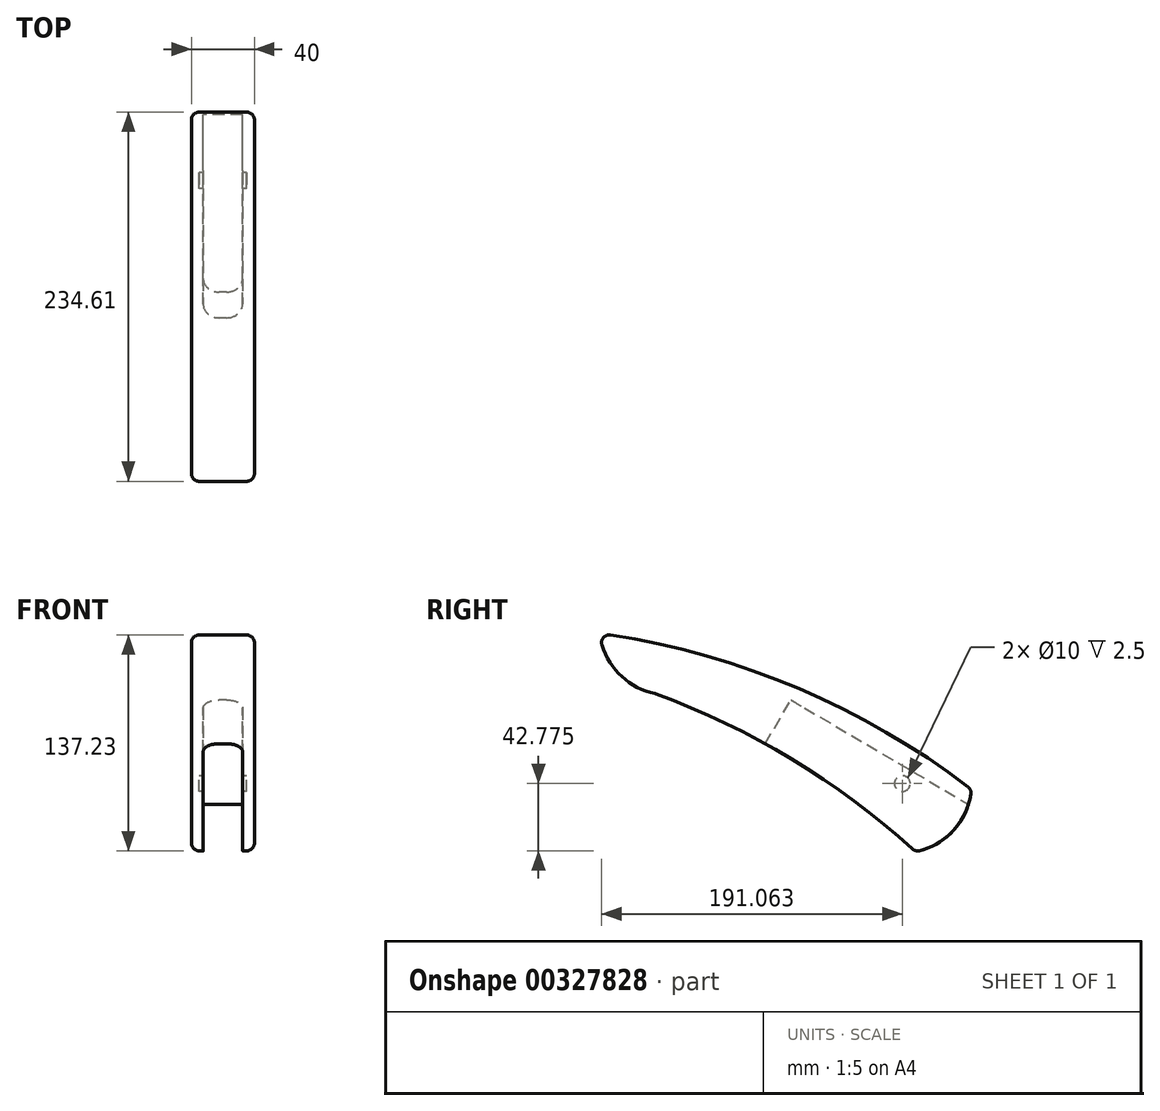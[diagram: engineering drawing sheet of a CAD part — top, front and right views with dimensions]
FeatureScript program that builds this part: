
annotation { "Feature Type Name" : "Feature", "Feature Type Description" : "" }
export const myFeature = defineFeature(function(context is Context, id is Id, definition is map)
    precondition{}
    {
        {
            var Q0;
            Q0=qCreatedBy(makeId("Right.planeOp"),FACE);
            var sketch = newSketch(context, id + "F0", { "sketchPlane" : qUnion([Q0])});
            skLineSegment(sketch, "E0.bottom", {"start": v(-93.5, -201.38) * mm, "end": v(36.5, -201.38) * mm});
            skLineSegment(sketch, "E0.top", {"start": v(-93.5, 198.62) * mm, "end": v(36.5, 198.62) * mm});
            skLineSegment(sketch, "E0.left", {"start": v(-93.5, -201.38) * mm, "end": v(-93.5, 198.62) * mm});
            skLineSegment(sketch, "E0.right", {"start": v(36.5, -201.38) * mm, "end": v(36.5, 198.62) * mm});
            skCircle(sketch, "E1", {"center": v(-63.5, -21.38) * mm, "radius": 5 * mm});
            skCircle(sketch, "E2", {"center": v(-13.5, 168.62) * mm, "radius": 5 * mm});
            skLineSegment(sketch, "E3", {"start": v(-63.5, -21.38) * mm, "end": v(-15.78, 249.23) * mm, "construction": true});
            skSolve(sketch);
        }
        {
            var Q0;
            Q0=makeQuery(id+"F0.imprint","IMPRINT",FACE,{"disambiguationData":[TD([[makeQuery(id+"F0.imprint","IMPRINT",EDGE,{"derivedFrom":sQuery(id+"F0.wireOp",EDGE,"E0.bottom")}),1.0]])]});
            var sketch = newSketch(context, id + "F1", { "sketchPlane" : qUnion([Q0])});
            skArc(sketch, "E4", {"start": v(-83.4, -179.38) * mm, "mid": v(-76.66, -2.28) * mm, "end": v(-91.76, 174.32) * mm});
            skArc(sketch, "E5", {"start": v(-4.63, -188.02) * mm, "mid": v(29.08, -8.61) * mm, "end": v(7.29, 172.63) * mm});
            skArc(sketch, "E6", {"start": v(-7.3, 186.7) * mm, "mid": v(-38.5, 193.04) * mm, "end": v(-70.09, 197.16) * mm});
            skPoint(sketch, "E7.orphan", {"position": v(0, 196.75) * mm});
            skPoint(sketch, "E8.orphan", {"position": v(0, -174.33) * mm});
            skPoint(sketch, "E9.visualSharp", {"position": v(-10.38, -203.65) * mm});
            skArc(sketch, "E9.filletArc", {"start": v(-23.5, -201.38) * mm, "mid": v(-11.94, -197.7) * mm, "end": v(-4.63, -188.02) * mm});
            skPoint(sketch, "E10.visualSharp", {"position": v(4.05, 183.8) * mm});
            skArc(sketch, "E10.filletArc", {"start": v(7.29, 172.63) * mm, "mid": v(1.9, 181.64) * mm, "end": v(-7.3, 186.7) * mm});
            skPoint(sketch, "E11.visualSharp", {"position": v(-95.6, 198.84) * mm});
            skArc(sketch, "E11.filletArc", {"start": v(-70.09, 197.16) * mm, "mid": v(-86.48, 191.01) * mm, "end": v(-91.76, 174.32) * mm});
            skPoint(sketch, "E12.visualSharp", {"position": v(-89.2, -228.69) * mm});
            skArc(sketch, "E12.filletArc", {"start": v(-83.4, -179.38) * mm, "mid": v(-78.33, -194.8) * mm, "end": v(-63.5, -201.38) * mm});
            skLineSegment(sketch, "E13", {"start": v(-63.5, -201.38) * mm, "end": v(-23.5, -201.38) * mm});
            skSolve(sketch);
        }
        {
            var Q0;
            Q0=makeQuery(id+"F0.imprint","IMPRINT",FACE,{"disambiguationData":[TD([[makeQuery(id+"F0.imprint","IMPRINT",EDGE,{"derivedFrom":sQuery(id+"F0.wireOp",EDGE,"E0.bottom")}),1.0]])]});
            var sketch = newSketch(context, id + "F2", { "sketchPlane" : qUnion([Q0])});
            skArc(sketch, "E14", {"start": v(-5.24, 125.4) * mm, "mid": v(-82.88, 183.6) * mm, "end": v(-170.3, 225.71) * mm});
            skArc(sketch, "E15", {"start": v(30.35, 164.93) * mm, "mid": v(-81.33, 229.89) * mm, "end": v(-205.92, 264.07) * mm});
            skArc(sketch, "E16", {"start": v(-205.92, 264.07) * mm, "mid": v(-194.3, 239.14) * mm, "end": v(-170.3, 225.71) * mm});
            skCircle(sketch, "E17", {"center": v(-13.5, 168.62) * mm, "radius": 5 * mm, "construction": true});
            skArc(sketch, "E18", {"start": v(-5.24, 125.4) * mm, "mid": v(19.2, 139.18) * mm, "end": v(30.35, 164.93) * mm});
            skPoint(sketch, "E19.orphan", {"position": v(0, 120.54) * mm});
            skSolve(sketch);
        }
        {
            var Q0;
            Q0=makeQuery(id+"F2.imprint","IMPRINT",FACE,{"disambiguationData":[TD([[makeQuery(id+"F2.imprint","IMPRINT",EDGE,{"derivedFrom":makeQuery(id+"F0.imprint","IMPRINT",EDGE,{"derivedFrom":sQuery(id+"F0.wireOp",EDGE,"E2")})}),1.0]])]});
            var Q1;
            {var subQ0=sQuery(id+"F2.wireOp",EDGE,"vNOhyl8z-5HtI-Y5xh-fr09-2KdCwjozxGuU");Q1=makeQuery(id+"F2.imprint","IMPRINT",FACE,{"disambiguationData":[TD([[makeQuery(id+"F2.imprint","IMPRINT",EDGE,{"derivedFrom":subQ0}),1.0]])]});}
            var Q2;
            {var subQ0=sQuery(id+"F2.wireOp",EDGE,"E16");Q2=makeQuery(id+"F2.imprint","IMPRINT",FACE,{"disambiguationData":[TD([[makeQuery(id+"F2.imprint","IMPRINT",EDGE,{"derivedFrom":subQ0}),1.0]])]});}
            var Q3;
            Q3=makeQuery(id+"F2.imprint","IMPRINT",FACE,{"disambiguationData":[TD([[makeQuery(id+"F2.imprint","IMPRINT",EDGE,{"derivedFrom":makeQuery(id+"F0.imprint","IMPRINT",EDGE,{"derivedFrom":sQuery(id+"F0.wireOp",EDGE,"E2")})}),-1.0]])]});
            extrude(context, id + "F3", {"entities" : qUnion([Q0, Q1, Q2, Q3]), "endBound" : BoundingType.SYMMETRIC, "depth" : 40 * mm, "offsetDistance" : 25 * mm});
        }
        {
            var Q0;
            Q0=makeQuery(id+"F3.opExtrude","CAP_FACE",FACE,{"disambiguationData":[OSD([sQuery(id+"F2.wireOp",EDGE,"E14"),sQuery(id+"F2.wireOp",EDGE,"E15"),sQuery(id+"F2.wireOp",EDGE,"E16"),sQuery(id+"F2.wireOp",EDGE,"vNOhyl8z-5HtI-Y5xh-fr09-2KdCwjozxGuU")])],"isStart":false});
            var Q1;
            Q1=makeQuery(id+"F3.opExtrude","CAP_FACE",FACE,{"disambiguationData":[OSD([sQuery(id+"F2.wireOp",EDGE,"E14"),sQuery(id+"F2.wireOp",EDGE,"E15"),sQuery(id+"F2.wireOp",EDGE,"E16"),sQuery(id+"F2.wireOp",EDGE,"vNOhyl8z-5HtI-Y5xh-fr09-2KdCwjozxGuU")])],"isStart":true});
            var Q2;
            Q2=makeQuery(id+"F3.opExtrude","SWEPT_EDGE",EDGE,{"disambiguationData":[OSD([sQuery(id+"F2.wireOp",EDGE,"E15"),sQuery(id+"F2.wireOp",EDGE,"vNOhyl8z-5HtI-Y5xh-fr09-2KdCwjozxGuU")])]});
            var Q3;
            Q3=makeQuery(id+"F3.opExtrude","SWEPT_EDGE",EDGE,{"disambiguationData":[OSD([sQuery(id+"F2.wireOp",EDGE,"E15"),sQuery(id+"F2.wireOp",EDGE,"E16")])]});
            var Q4;
            Q4=makeQuery(id+"F3.opExtrude","SWEPT_EDGE",EDGE,{"disambiguationData":[OSD([sQuery(id+"F2.wireOp",EDGE,"E14"),sQuery(id+"F2.wireOp",EDGE,"E16")])]});
            var Q5;
            Q5=makeQuery(id+"F3.opExtrude","SWEPT_EDGE",EDGE,{"disambiguationData":[OSD([sQuery(id+"F2.wireOp",EDGE,"E14"),sQuery(id+"F2.wireOp",EDGE,"vNOhyl8z-5HtI-Y5xh-fr09-2KdCwjozxGuU")])]});
            fillet(context, id + "F4", {"entities" : qUnion([Q0, Q1, Q2, Q3, Q4, Q5]), "radius" : 5 * mm, "tangentPropagation" : true, "allowEdgeOverflow" : false});
        }
        {
            var Q0;
            Q0=makeQuery(id+"F0.imprint","IMPRINT",FACE,{"disambiguationData":[TD([[makeQuery(id+"F0.imprint","IMPRINT",EDGE,{"derivedFrom":sQuery(id+"F0.wireOp",EDGE,"E0.bottom")}),1.0]])]});
            var sketch = newSketch(context, id + "F5", { "sketchPlane" : qUnion([Q0])});
            skCircle(sketch, "E20.0", {"center": v(-13.5, 168.62) * mm, "radius": 5 * mm});
            skSolve(sketch);
        }
        {
            var Q0;
            Q0 = qSketchRegion(id + "F5", true);
            extrude(context, id + "F6", {"entities" : qUnion([Q0]), "operationType" : NewBodyOperationType.REMOVE, "endBound" : BoundingType.SYMMETRIC, "depth" : 30 * mm, "offsetDistance" : 25 * mm});
        }
        {
            var Q0;
            Q0=makeQuery(id+"F3.opExtrude","CAP_FACE",FACE,{"disambiguationData":[OSD([sQuery(id+"F2.wireOp",EDGE,"E14"),sQuery(id+"F2.wireOp",EDGE,"E15"),sQuery(id+"F2.wireOp",EDGE,"E16"),sQuery(id+"F2.wireOp",EDGE,"E18")])],"isStart":false});
            cPlane(context, id + "F7", {"entities" : qUnion([Q0]), "cplaneType" : CPlaneType.OFFSET, "offset" : 20 * mm, "oppositeDirection" : true, "width" : 150 * mm, "height" : 150 * mm});
        }
        {
            var Q0;
            Q0=qCreatedBy(id+"F7.planeOp",FACE);
            var sketch = newSketch(context, id + "F8", { "sketchPlane" : qUnion([Q0])});
            skLineSegment(sketch, "E21", {"start": v(-100.93, 193.45) * mm, "end": v(-84.28, 221.76) * mm});
            skLineSegment(sketch, "E22", {"start": v(-84.28, 221.76) * mm, "end": v(32.27, 153.2) * mm});
            skLineSegment(sketch, "E23", {"start": v(32.27, 153.2) * mm, "end": v(5.4, 111.61) * mm});
            skLineSegment(sketch, "E24", {"start": v(5.4, 111.61) * mm, "end": v(-109.68, 179.31) * mm});
            skLineSegment(sketch, "E25", {"start": v(-109.68, 179.31) * mm, "end": v(-100.93, 193.45) * mm});
            skSolve(sketch);
        }
        {
            var Q0;
            Q0 = qSketchRegion(id + "F8", true);
            extrude(context, id + "F9", {"entities" : qUnion([Q0]), "operationType" : NewBodyOperationType.REMOVE, "endBound" : BoundingType.SYMMETRIC, "depth" : 25 * mm, "offsetDistance" : 25 * mm});
        }
        {
            var Q0;
            Q0=makeQuery(id+"F9.boolean.opBoolean","COPY",EDGE,{"derivedFrom":makeQuery(id+"F9.opExtrude","CAP_EDGE",EDGE,{"disambiguationData":[OSD([sQuery(id+"F8.wireOp",EDGE,"E21")])],"isStart":true})});
            var Q1;
            Q1=makeQuery(id+"F9.boolean.opBoolean","COPY",EDGE,{"derivedFrom":makeQuery(id+"F9.opExtrude","CAP_EDGE",EDGE,{"disambiguationData":[OSD([sQuery(id+"F8.wireOp",EDGE,"E21")])],"isStart":false})});
            fillet(context, id + "F10", {"entities" : qUnion([Q0, Q1]), "radius" : 10 * mm, "tangentPropagation" : true, "allowEdgeOverflow" : false});
        }
    });
